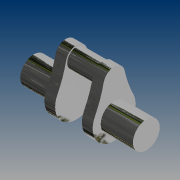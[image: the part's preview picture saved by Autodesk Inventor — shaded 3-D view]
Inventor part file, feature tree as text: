
AUTODESK INVENTOR PART (.ipt)
format: ipt  version: 2015 (Build 190159000, 159)  size: 125,440 bytes
history: native  units: mm
features: extrude x3, sketch x3, mirror x2, plane x1
ambient origin geometry x8: Origin, YZ Plane, XZ Plane, XY Plane, X Axis, Y Axis, Z Axis, Center Point
bodies: Body1 (feature_tree)
feature tree (9):
  extrude  "Extrusion4"  Depth=40.0mm
  extrude  "Extrusion5"  Depth=200.0mm
  extrude  "Extrusion6"  Depth=20.0mm TaperAngle=0.0deg
  plane  "Work Plane2"
  mirror  "Mirror3"
  mirror  "Mirror4"
  sketch  "Sketch4"  dims[d13=80.0mm d14=40.0mm]
  sketch  "Sketch5"  dims[d15=60.0mm d16=200.0mm]
  sketch  "Sketch6"  dims[d17=200.0mm d18=20.0mm d19=0.0mm d20=50.0mm d21=60.0mm d22=0.0mm d23=35.0mm d24=50.0mm d25=0.0mm]
